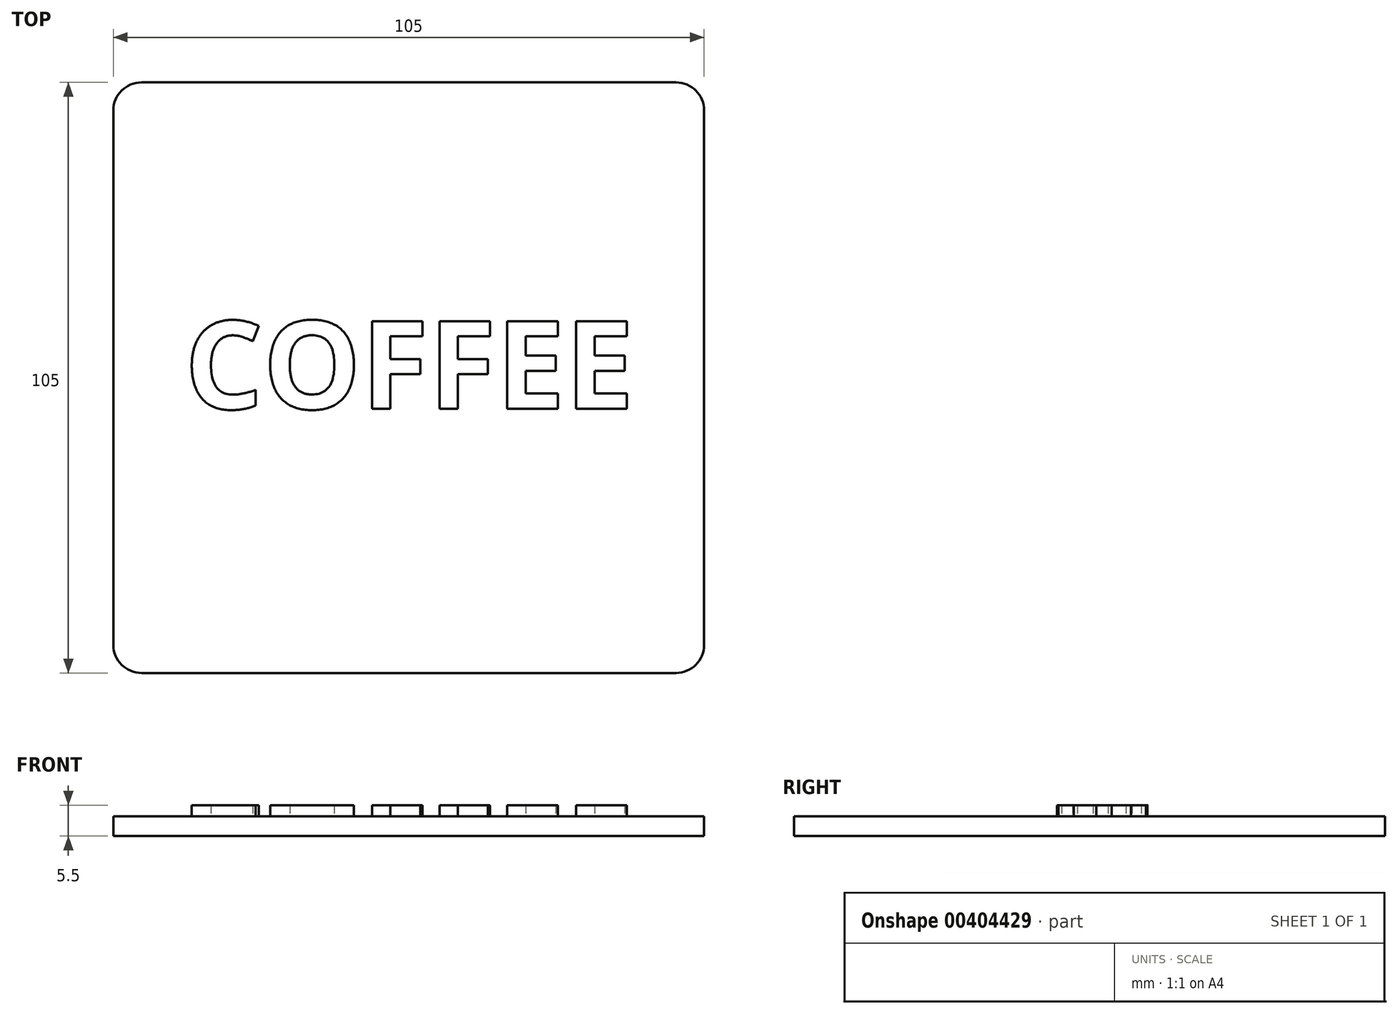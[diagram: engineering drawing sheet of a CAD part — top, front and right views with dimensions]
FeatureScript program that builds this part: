
annotation { "Feature Type Name" : "Feature", "Feature Type Description" : "" }
export const myFeature = defineFeature(function(context is Context, id is Id, definition is map)
    precondition{}
    {
        {
            var Q0;
            Q0=qCreatedBy(makeId("Top.planeOp"),FACE);
            var sketch = newSketch(context, id + "F0", { "sketchPlane" : qUnion([Q0])});
            skLineSegment(sketch, "E0.bottom", {"start": v(47.5, -52.5) * mm, "end": v(-47.5, -52.5) * mm});
            skLineSegment(sketch, "E0.top", {"start": v(47.5, 52.5) * mm, "end": v(-47.5, 52.5) * mm});
            skLineSegment(sketch, "E0.left", {"start": v(52.5, -47.5) * mm, "end": v(52.5, 47.5) * mm});
            skLineSegment(sketch, "E0.right", {"start": v(-52.5, -47.5) * mm, "end": v(-52.5, 47.5) * mm});
            skPoint(sketch, "E0.middle", {"position": v(0, 0) * mm});
            skPoint(sketch, "E1", {"position": v(-52.5, 47.5) * mm});
            skPoint(sketch, "E2", {"position": v(-47.5, 52.5) * mm});
            skPoint(sketch, "E3", {"position": v(47.5, 52.5) * mm});
            skPoint(sketch, "E4", {"position": v(52.5, 47.5) * mm});
            skPoint(sketch, "E5", {"position": v(52.5, -47.5) * mm});
            skPoint(sketch, "E6", {"position": v(47.5, -52.5) * mm});
            skPoint(sketch, "E7", {"position": v(-52.5, -47.5) * mm});
            skPoint(sketch, "E8", {"position": v(-47.5, -52.5) * mm});
            skArc(sketch, "E9", {"start": v(-47.5, 52.5) * mm, "mid": v(-51.04, 51.04) * mm, "end": v(-52.5, 47.5) * mm});
            skArc(sketch, "E10", {"start": v(52.5, 47.5) * mm, "mid": v(51.04, 51.04) * mm, "end": v(47.5, 52.5) * mm});
            skArc(sketch, "E11", {"start": v(-52.5, -47.5) * mm, "mid": v(-51.04, -51.04) * mm, "end": v(-47.5, -52.5) * mm});
            skArc(sketch, "E12", {"start": v(47.5, -52.5) * mm, "mid": v(51.04, -51.04) * mm, "end": v(52.5, -47.5) * mm});
            skPoint(sketch, "E13.orphan", {"position": v(-52.5, 52.5) * mm});
            skPoint(sketch, "E14.orphan", {"position": v(52.5, 52.5) * mm});
            skPoint(sketch, "E15.orphan", {"position": v(52.5, -52.5) * mm});
            skPoint(sketch, "E16.orphan", {"position": v(-52.5, -52.5) * mm});
            skSolve(sketch);
        }
        {
            var Q0;
            Q0 = qSketchRegion(id + "F0", true);
            extrude(context, id + "F1", {"entities" : qUnion([Q0]), "depth" : 3.5 * mm});
        }
        {
            var Q0;
            Q0=makeQuery(id+"F1.opExtrude","CAP_FACE",FACE,{"disambiguationData":[OSD([sQuery(id+"F0.wireOp",EDGE,"E0.bottom"),sQuery(id+"F0.wireOp",EDGE,"E0.top"),sQuery(id+"F0.wireOp",EDGE,"E0.left"),sQuery(id+"F0.wireOp",EDGE,"E0.right"),sQuery(id+"F0.wireOp",EDGE,"E9"),sQuery(id+"F0.wireOp",EDGE,"E10"),sQuery(id+"F0.wireOp",EDGE,"E11"),sQuery(id+"F0.wireOp",EDGE,"E12")])],"isStart":false});
            var sketch = newSketch(context, id + "F2", { "sketchPlane" : qUnion([Q0])});
            skText(sketch, "E17", { "text": "COFFEE", "fontName": "OpenSans-Bold.ttf"});
            const initialGuessF2  = {"E17": [-0.03983, -0.00556, 1, 0, 0.01575]};
            skSetInitialGuess(sketch, initialGuessF2);
            skSolve(sketch);
        }
        {
            var Q0;
            Q0 = qSketchRegion(id + "F2", true);
            extrude(context, id + "F3", {"entities" : qUnion([Q0]), "operationType" : NewBodyOperationType.ADD, "depth" : 2 * mm});
        }
    });
